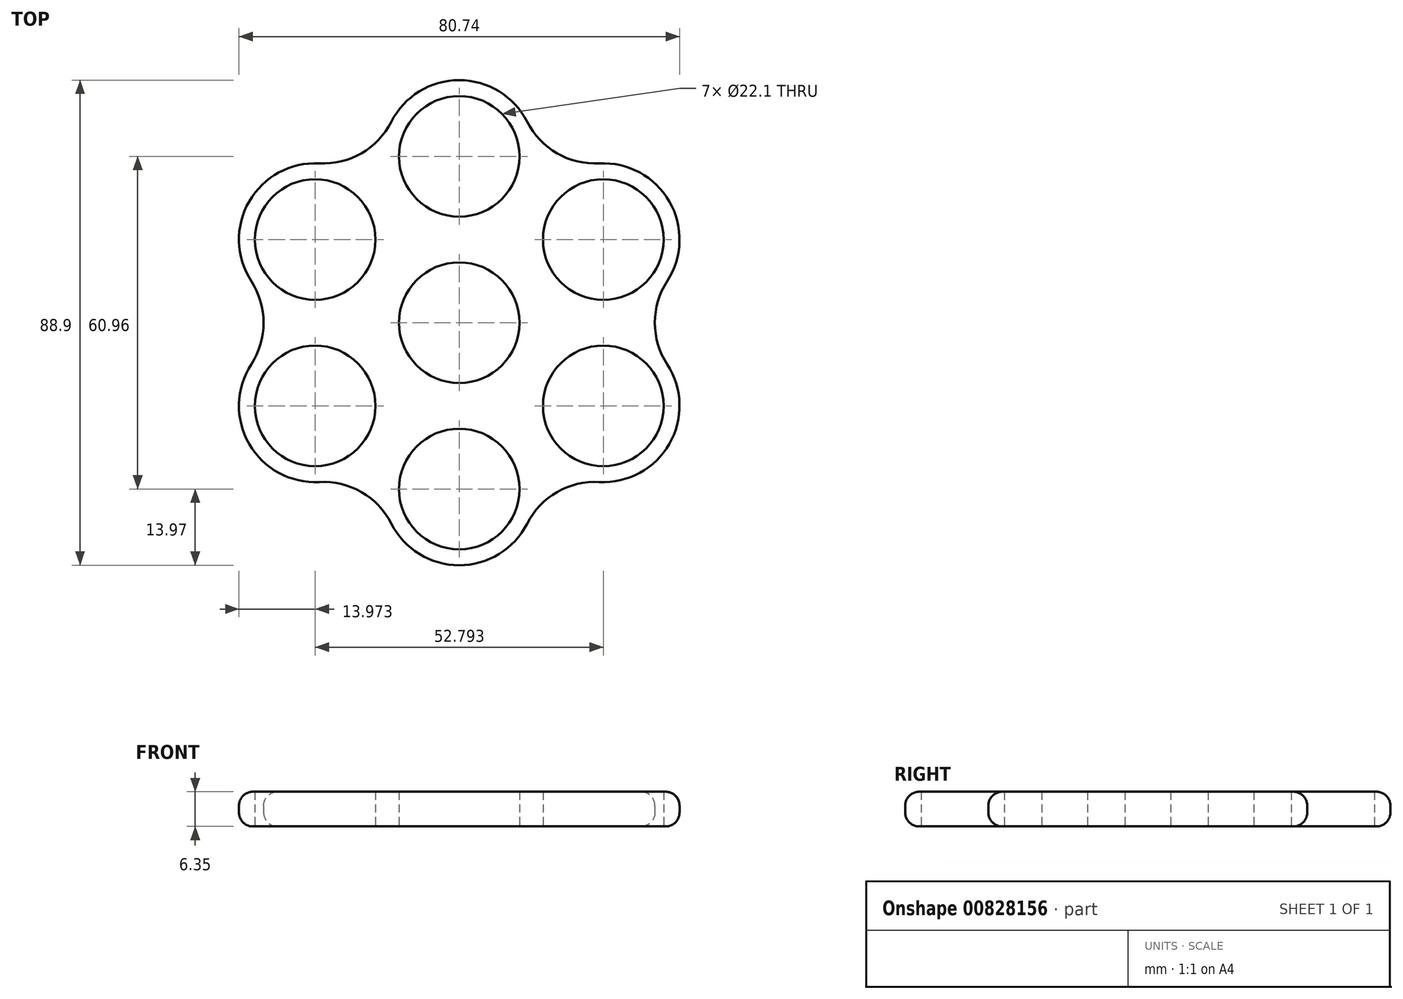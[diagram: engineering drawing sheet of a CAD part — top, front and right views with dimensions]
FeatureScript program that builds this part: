
annotation { "Feature Type Name" : "Feature", "Feature Type Description" : "" }
export const myFeature = defineFeature(function(context is Context, id is Id, definition is map)
    precondition{}
    {
        {
            var Q0;
            Q0=qCreatedBy(makeId("Top.planeOp"),FACE);
            var sketch = newSketch(context, id + "F0", { "sketchPlane" : qUnion([Q0])});
            skCircle(sketch, "E0", {"center": v(0, 0) * mm, "radius": 11.05 * mm});
            skCircle(sketch, "E1", {"center": v(0, 30.48) * mm, "radius": 11.05 * mm});
            skArc(sketch, "E2", {"start": v(12.45, 36.82) * mm, "mid": v(0, 44.45) * mm, "end": v(-12.45, 36.82) * mm});
            skArc(sketch, "E3.1.0", {"start": v(-25.66, 29.2) * mm, "mid": v(-38.5, 22.22) * mm, "end": v(-38.11, 7.63) * mm});
            skCircle(sketch, "E3.1.1", {"center": v(-26.4, 15.24) * mm, "radius": 11.05 * mm});
            skArc(sketch, "E3.2.0", {"start": v(-38.11, -7.63) * mm, "mid": v(-38.5, -22.23) * mm, "end": v(-25.66, -29.2) * mm});
            skCircle(sketch, "E3.2.1", {"center": v(-26.4, -15.24) * mm, "radius": 11.05 * mm});
            skArc(sketch, "E3.3.0", {"start": v(-12.45, -36.82) * mm, "mid": v(0, -44.45) * mm, "end": v(12.45, -36.82) * mm});
            skCircle(sketch, "E3.3.1", {"center": v(0, -30.48) * mm, "radius": 11.05 * mm});
            skArc(sketch, "E3.4.0", {"start": v(25.66, -29.2) * mm, "mid": v(38.5, -22.23) * mm, "end": v(38.11, -7.63) * mm});
            skCircle(sketch, "E3.4.1", {"center": v(26.4, -15.24) * mm, "radius": 11.05 * mm});
            skArc(sketch, "E3.5.0", {"start": v(38.11, 7.63) * mm, "mid": v(38.5, 22.23) * mm, "end": v(25.66, 29.2) * mm});
            skCircle(sketch, "E3.5.1", {"center": v(26.4, 15.24) * mm, "radius": 11.05 * mm});
            skLineSegment(sketch, "E4", {"start": v(0, 0) * mm, "end": v(24.93, 43.18) * mm});
            skArc(sketch, "E5", {"start": v(12.45, 36.82) * mm, "mid": v(17.93, 31.05) * mm, "end": v(25.66, 29.2) * mm});
            skArc(sketch, "E6.1.0", {"start": v(-25.66, 29.2) * mm, "mid": v(-17.93, 31.05) * mm, "end": v(-12.45, 36.82) * mm});
            skArc(sketch, "E6.2.0", {"start": v(-38.11, -7.63) * mm, "mid": v(-35.85, 0) * mm, "end": v(-38.11, 7.63) * mm});
            skArc(sketch, "E6.3.0", {"start": v(-12.45, -36.82) * mm, "mid": v(-17.93, -31.05) * mm, "end": v(-25.66, -29.2) * mm});
            skArc(sketch, "E6.4.0", {"start": v(25.66, -29.2) * mm, "mid": v(17.93, -31.05) * mm, "end": v(12.45, -36.82) * mm});
            skArc(sketch, "E6.5.0", {"start": v(38.11, 7.63) * mm, "mid": v(35.85, 0) * mm, "end": v(38.11, -7.63) * mm});
            skSolve(sketch);
        }
        {
            var Q0;
            Q0=makeQuery(id+"F0.imprint","IMPRINT",FACE,{"disambiguationData":[TD([[makeQuery(id+"F0.imprint","IMPRINT",EDGE,{"derivedFrom":sQuery(id+"F0.wireOp",EDGE,"E0")}),-1.0]])]});
            extrude(context, id + "F1", {"entities" : qUnion([Q0]), "depth" : 6.35 * mm, "offsetDistance" : 25.4 * mm});
        }
        {
            var Q0;
            Q0=makeQuery(id+"F1.opExtrude","CAP_EDGE",EDGE,{"disambiguationData":[OSD([sQuery(id+"F0.wireOp",EDGE,"E3.3.0")])],"isStart":false});
            fillet(context, id + "F2", {"entities" : qUnion([Q0]), "radius" : 2.54 * mm, "tangentPropagation" : true, "allowEdgeOverflow" : false});
        }
        {
            var Q0;
            Q0=makeQuery(id+"F1.opExtrude","CAP_EDGE",EDGE,{"disambiguationData":[OSD([sQuery(id+"F0.wireOp",EDGE,"E6.3.0")])],"isStart":true});
            fillet(context, id + "F3", {"entities" : qUnion([Q0]), "radius" : 2.54 * mm, "tangentPropagation" : true, "allowEdgeOverflow" : false});
        }
    });
